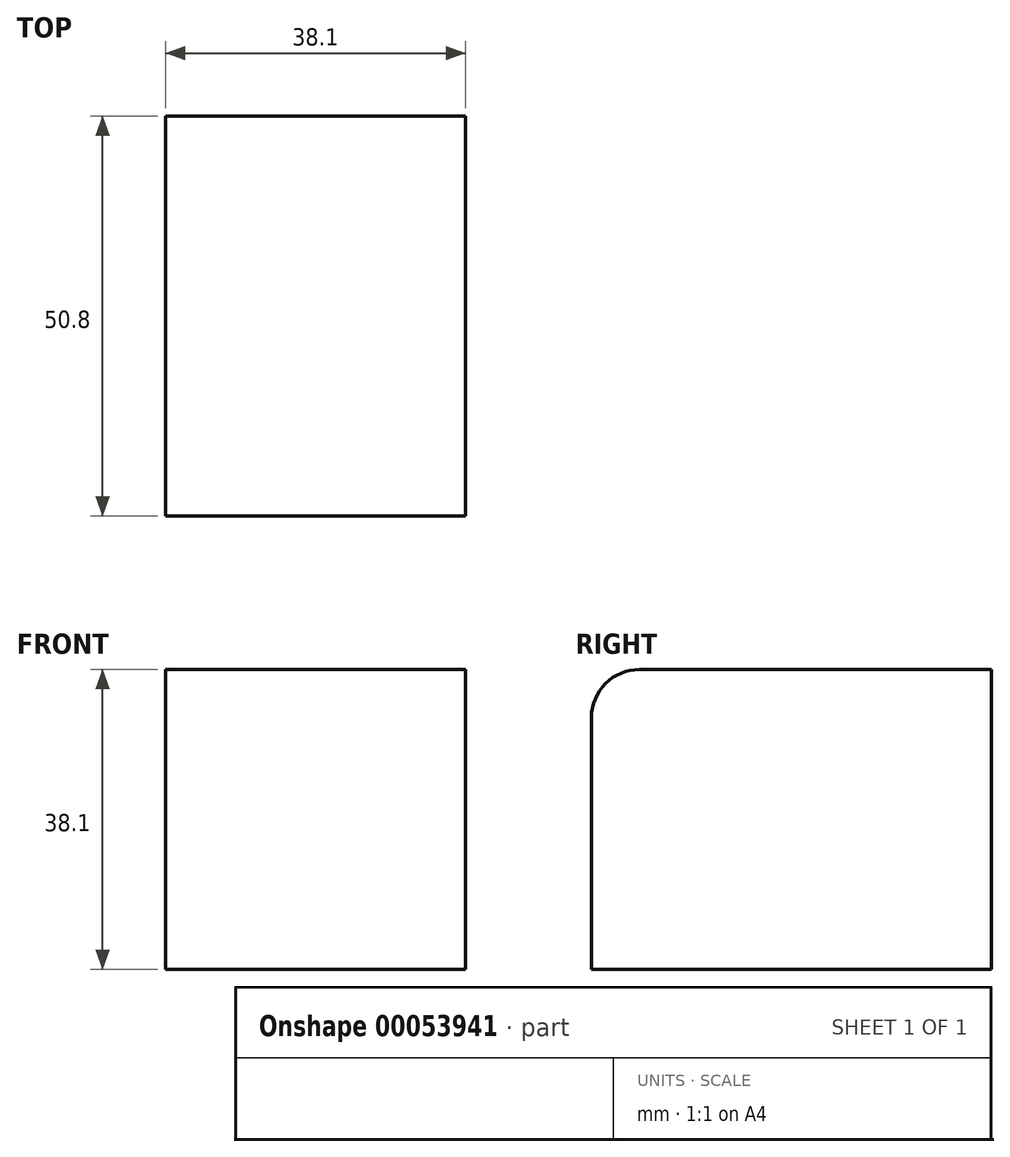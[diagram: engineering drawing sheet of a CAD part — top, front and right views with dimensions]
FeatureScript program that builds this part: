
annotation { "Feature Type Name" : "Feature", "Feature Type Description" : "" }
export const myFeature = defineFeature(function(context is Context, id is Id, definition is map)
    precondition{}
    {
        {
            var Q0;
            Q0=qCreatedBy(makeId("Front.planeOp"),FACE);
            var sketch = newSketch(context, id + "F0", { "sketchPlane" : qUnion([Q0])});
            skLineSegment(sketch, "E0.bottom", {"start": v(-52.85, 28.09) * mm, "end": v(-14.75, 28.09) * mm});
            skLineSegment(sketch, "E0.top", {"start": v(-52.85, -10.01) * mm, "end": v(-14.75, -10.01) * mm});
            skLineSegment(sketch, "E0.left", {"start": v(-52.85, 28.09) * mm, "end": v(-52.85, -10.01) * mm});
            skLineSegment(sketch, "E0.right", {"start": v(-14.75, 28.09) * mm, "end": v(-14.75, -10.01) * mm});
            skSolve(sketch);
        }
        {
            var Q0;
            Q0=makeQuery(id+"F0.imprint","IMPRINT",FACE,{"disambiguationData":[TD([[makeQuery(id+"F0.imprint","IMPRINT",EDGE,{"derivedFrom":sQuery(id+"F0.wireOp",EDGE,"E0.bottom")}),-1.0]])]});
            extrude(context, id + "F1", {"entities" : qUnion([Q0]), "depth" : 50.8 * mm});
        }
        {
            var Q0;
            Q0=makeQuery(id+"F1.opExtrude","CAP_EDGE",EDGE,{"disambiguationData":[OSD([sQuery(id+"F0.wireOp",EDGE,"E0.bottom")])],"isStart":false});
            fillet(context, id + "F2", {"entities" : qUnion([Q0]), "radius" : 6.11 * mm, "tangentPropagation" : true, "allowEdgeOverflow" : false});
        }
    });
